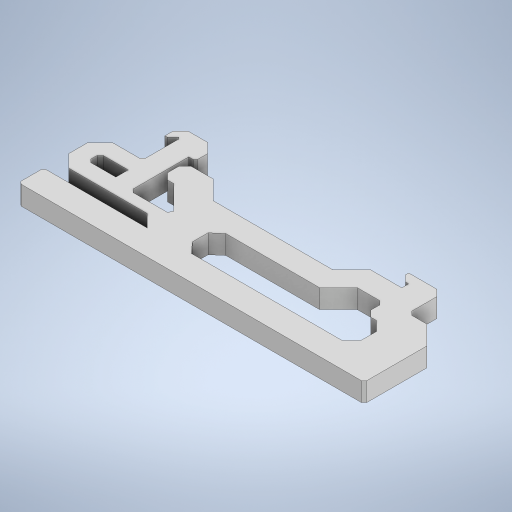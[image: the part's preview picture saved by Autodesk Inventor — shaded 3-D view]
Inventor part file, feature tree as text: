
AUTODESK INVENTOR PART (.ipt)
format: ipt  version: 2023 (Build 270158000, 158)  size: 382,976 bytes
history: native  units: in
note: dims shown in document units (in); Inventor stores cm internally (conversion verified against a paired STEP export)
features: extrude x1, sketch x1
ambient origin geometry x8: Origin, YZ Plane, XZ Plane, XY Plane, X Axis, Y Axis, Z Axis, Center Point
bodies: Solid1 (feature_tree)
feature tree (2):
  extrude  "Extrusion1"  Depth=0.1566in
  sketch  "Sketch1"  dims[d2=0.3758in d3=0.1566in d4=0.1762in d6=0.1957in d7=0.1387in d9=0.1174in d11=0.0391in d12=0.0157in d13=2.1217in d14=0.0973in d15=0.0587in d16=0.0587in d18=0.0548in d19=0.0235in d20=0.9395in d21=0.0587in d22=0.0973in d23=0.5854in d24=0.1174in d25=0.7438in d27=0.1174in d28=0.1174in d29=0.137in d30=0.1475in d31=0.0277in d32=0.2143in d33=0.3464in d34=0.0196in d35=0.0626in d36=0.0137in d37=0.0274in d38=0.0607in d39=0.1213in d40=0.047in d41=0.0509in d42=0.0157in d43=0.0356in d44=0.0094in d45=0.2063in d46=0.0196in d47=0.1664in d48=0.0783in d49=0.1174in d50=0.0783in d51=0.4893in d52=0.0783in d54=0.6302in d55=0.0156in d56=0.1253in d58=0.1174in d59=0.1174in d60=0.1174in d61=0.0391in d62=0.0391in d63=0.0391in d64=0.1475in d66=0.0695in d67=0.0391in d68=0.0391in d69=0.0196in d75=0.0196in d76=0.0196in d77=0.0196in d78=0.0196in d89=0.0658in d90=0.0235in d91=0.0587in d92=0.0391in d93=0.0391in d94=0.0391in d95=0.0626in d96=0.0548in d97=0.0156in d98=0.0471in d99=0.0607in d100=0.0137in d101=0.0196in d103=0.094in d105=0.0196in d106=0.0156in d107=0.1376in d108=0.0352in d109=0.2349in d110=0.1566in d111=0.3568in d112=0.1566in d113=0.0115in d114=0.0156in d115=0.0772in d116=0.1751in d117=0.0984in d118=0.118in d119=0.1181in d120=0.0in]
